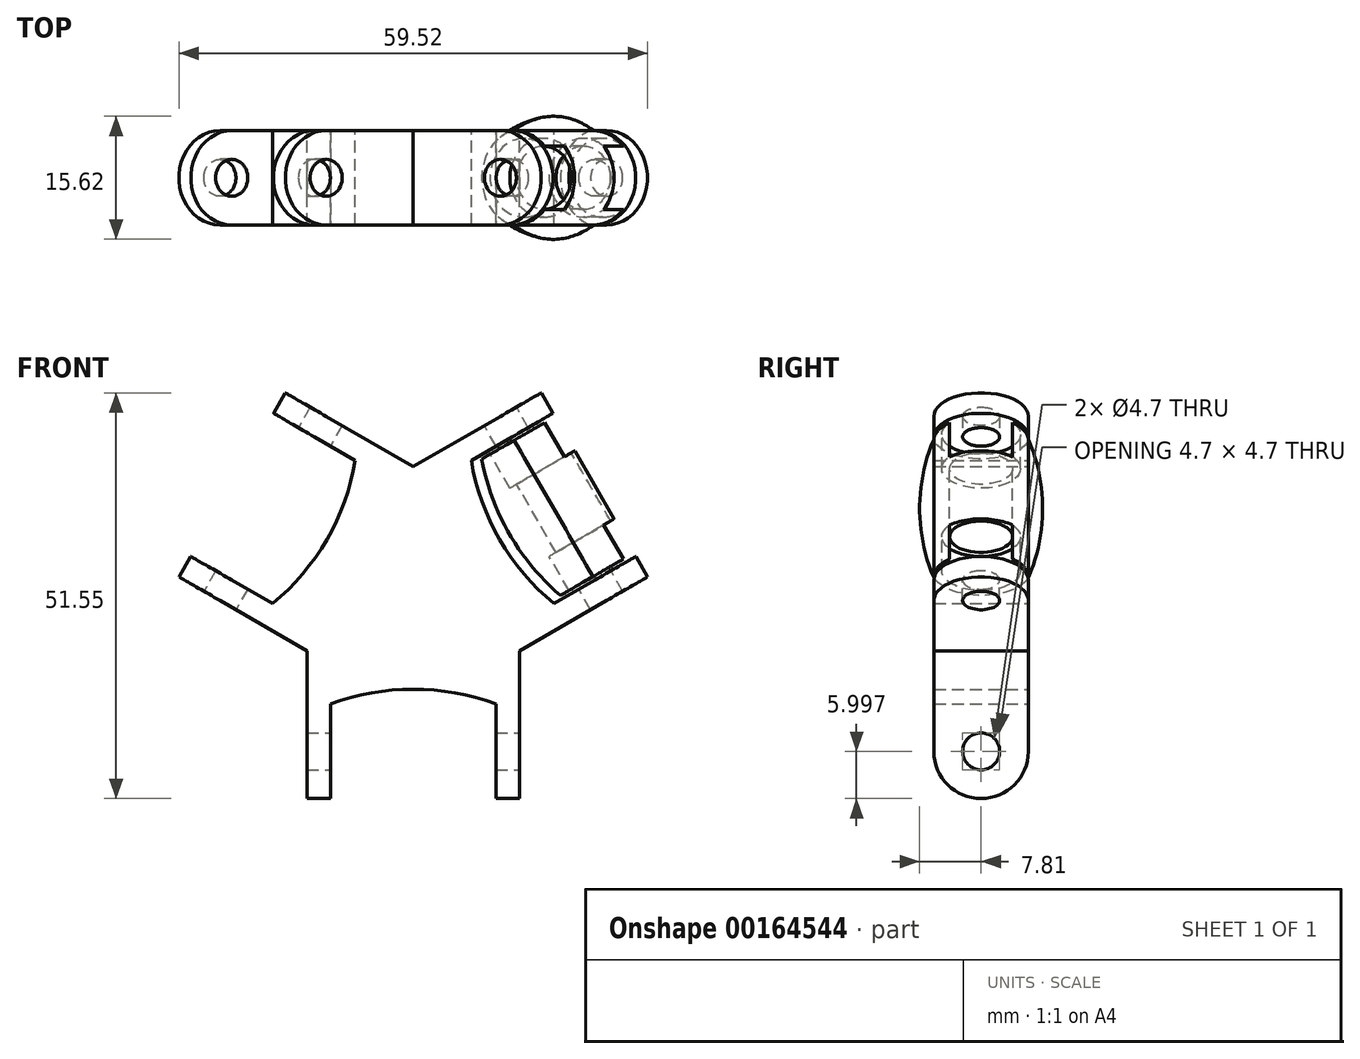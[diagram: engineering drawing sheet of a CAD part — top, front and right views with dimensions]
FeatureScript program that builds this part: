
annotation { "Feature Type Name" : "Feature", "Feature Type Description" : "" }
export const myFeature = defineFeature(function(context is Context, id is Id, definition is map)
    precondition{}
    {
        {
            var Q0;
            Q0=qCreatedBy(makeId("Front.planeOp"),FACE);
            var sketch = newSketch(context, id + "F0", { "sketchPlane" : qUnion([Q0])});
            skCircle(sketch, "E0", {"center": v(0, 0) * mm, "radius": 30 * mm, "construction": true});
            skLineSegment(sketch, "E1", {"start": v(0, 0) * mm, "end": v(0, 27.8) * mm, "construction": true});
            skLineSegment(sketch, "E2", {"start": v(0, 0) * mm, "end": v(24.85, -14.35) * mm, "construction": true});
            skLineSegment(sketch, "E3", {"start": v(38.06, 38.48) * mm, "end": v(52.36, 13.72) * mm, "construction": true});
            skLineSegment(sketch, "E4", {"start": v(0, 0) * mm, "end": v(45.2, 26.1) * mm, "construction": true});
            skLineSegment(sketch, "E5", {"start": v(17.76, 22.38) * mm, "end": v(8.6, 17.09) * mm});
            skLineSegment(sketch, "E6", {"start": v(28.26, 4.2) * mm, "end": v(19.1, -1.1) * mm});
            skArc(sketch, "E7", {"start": v(8.6, 17.09) * mm, "mid": v(12.2, 7.05) * mm, "end": v(19.1, -1.1) * mm, "construction": true});
            skLineSegment(sketch, "E8", {"start": v(19.09, 23.14) * mm, "end": v(24.34, 14.05) * mm, "construction": true});
            skLineSegment(sketch, "E9", {"start": v(24.34, 14.05) * mm, "end": v(29.59, 4.96) * mm, "construction": true});
            skLineSegment(sketch, "E10", {"start": v(13.84, 20.12) * mm, "end": v(24.34, 1.93) * mm, "construction": true});
            skLineSegment(sketch, "E11", {"start": v(13.5, -7.8) * mm, "end": v(21.63, -3.1) * mm, "construction": true});
            skLineSegment(sketch, "E12.MirrorCS", {"start": v(0, 15.59) * mm, "end": v(8.13, 20.28) * mm, "construction": true});
            skPoint(sketch, "E13.center", {"position": v(0.48, 0.8) * mm});
            skLineSegment(sketch, "E13.anchor1", {"start": v(0.48, 0.8) * mm, "end": v(0, 0) * mm, "construction": true});
            skLineSegment(sketch, "E13.anchor2", {"start": v(0.48, 0.8) * mm, "end": v(1.42, 0.8) * mm, "construction": true});
            skLineSegment(sketch, "E14", {"start": v(17.76, 22.38) * mm, "end": v(16.26, 24.98) * mm});
            skLineSegment(sketch, "E15", {"start": v(16.26, 24.98) * mm, "end": v(0, 15.59) * mm});
            skLineSegment(sketch, "E16", {"start": v(8.6, 17.09) * mm, "end": v(7.37, 16.38) * mm});
            skLineSegment(sketch, "E17", {"start": v(19.1, -1.1) * mm, "end": v(17.87, -1.8) * mm});
            skLineSegment(sketch, "E18", {"start": v(28.26, 4.2) * mm, "end": v(29.76, 1.6) * mm});
            skLineSegment(sketch, "E19", {"start": v(29.76, 1.6) * mm, "end": v(13.5, -7.8) * mm});
            skArc(sketch, "E20", {"start": v(7.37, 16.38) * mm, "mid": v(10.98, 6.34) * mm, "end": v(17.87, -1.8) * mm});
            skLineSegment(sketch, "E21.1.0", {"start": v(-29.76, 1.6) * mm, "end": v(-13.5, -7.8) * mm});
            skLineSegment(sketch, "E21.1.1", {"start": v(-28.26, 4.2) * mm, "end": v(-29.76, 1.6) * mm});
            skLineSegment(sketch, "E21.1.2", {"start": v(-28.26, 4.2) * mm, "end": v(-19.1, -1.1) * mm});
            skLineSegment(sketch, "E21.1.3", {"start": v(-19.1, -1.1) * mm, "end": v(-17.87, -1.8) * mm});
            skArc(sketch, "E21.1.4", {"start": v(-17.87, -1.8) * mm, "mid": v(-10.98, 6.34) * mm, "end": v(-7.37, 16.38) * mm});
            skLineSegment(sketch, "E21.1.5", {"start": v(-8.6, 17.09) * mm, "end": v(-7.37, 16.38) * mm});
            skLineSegment(sketch, "E21.1.6", {"start": v(-17.76, 22.38) * mm, "end": v(-8.6, 17.09) * mm});
            skLineSegment(sketch, "E21.1.7", {"start": v(-17.76, 22.38) * mm, "end": v(-16.26, 24.98) * mm});
            skLineSegment(sketch, "E21.1.8", {"start": v(-16.26, 24.98) * mm, "end": v(0, 15.59) * mm});
            skLineSegment(sketch, "E21.2.0", {"start": v(13.5, -26.57) * mm, "end": v(13.5, -7.8) * mm});
            skLineSegment(sketch, "E21.2.1", {"start": v(10.5, -26.57) * mm, "end": v(13.5, -26.57) * mm});
            skLineSegment(sketch, "E21.2.2", {"start": v(10.5, -26.57) * mm, "end": v(10.5, -16) * mm});
            skLineSegment(sketch, "E21.2.3", {"start": v(10.5, -16) * mm, "end": v(10.5, -14.57) * mm});
            skArc(sketch, "E21.2.4", {"start": v(10.5, -14.57) * mm, "mid": v(0, -12.68) * mm, "end": v(-10.5, -14.57) * mm});
            skLineSegment(sketch, "E21.2.5", {"start": v(-10.5, -16) * mm, "end": v(-10.5, -14.57) * mm});
            skLineSegment(sketch, "E21.2.6", {"start": v(-10.5, -26.57) * mm, "end": v(-10.5, -16) * mm});
            skLineSegment(sketch, "E21.2.7", {"start": v(-10.5, -26.57) * mm, "end": v(-13.5, -26.57) * mm});
            skLineSegment(sketch, "E21.2.8", {"start": v(-13.5, -26.57) * mm, "end": v(-13.5, -7.8) * mm});
            skSolve(sketch);
        }
        {
            var Q0;
            Q0=qCreatedBy(makeId("Front.planeOp"),FACE);
            var sketch = newSketch(context, id + "F1", { "sketchPlane" : qUnion([Q0])});
            skLineSegment(sketch, "E22.0", {"start": v(13.84, 20.12) * mm, "end": v(24.34, 1.93) * mm, "construction": true});
            skLineSegment(sketch, "E23.0", {"start": v(19.76, -0.14) * mm, "end": v(17.26, 4.2) * mm});
            skArc(sketch, "E23.1", {"start": v(8.7, 16.57) * mm, "mid": v(12.2, 7.05) * mm, "end": v(18.7, -0.75) * mm});
            skLineSegment(sketch, "E24.trimOffspring", {"start": v(9.76, 17.18) * mm, "end": v(8.7, 16.57) * mm});
            skLineSegment(sketch, "E25.trimOffspring", {"start": v(19.76, -0.14) * mm, "end": v(18.7, -0.75) * mm});
            skLineSegment(sketch, "E26", {"start": v(12.26, 12.85) * mm, "end": v(13.13, 13.35) * mm});
            skLineSegment(sketch, "E27", {"start": v(13.13, 13.35) * mm, "end": v(18.13, 4.7) * mm});
            skLineSegment(sketch, "E28", {"start": v(18.13, 4.7) * mm, "end": v(17.26, 4.2) * mm});
            skLineSegment(sketch, "E29.trimOffspring", {"start": v(12.26, 12.85) * mm, "end": v(9.76, 17.18) * mm});
            skPoint(sketch, "E30.orphan", {"position": v(8.6, 17.09) * mm});
            skSolve(sketch);
        }
        {
            var Q0;
            Q0=qSketchRegion(id+"F1",true);
            var Q1;
            Q1=sQuery(id+"F1.wireOp",EDGE,"E22.0");
            revolve(context, id + "F2", {"entities" : qUnion([Q0]), "axis" : qUnion([Q1]), "revolveType" : RevolveType.FULL});
        }
        {
            var Q0;
            Q0=qSketchRegion(id+"F0",true);
            extrude(context, id + "F3", {"entities" : qUnion([Q0]), "endBound" : BoundingType.SYMMETRIC, "depth" : 12 * mm});
        }
        {
            var Q0;
            Q0=makeQuery(id+"F3.opExtrude","SWEPT_FACE",FACE,{"disambiguationData":[OSD([sQuery(id+"F0.wireOp",EDGE,"E15")])]});
            var sketch = newSketch(context, id + "F4", { "sketchPlane" : qUnion([Q0])});
            skArc(sketch, "E31", {"start": v(20.57, -6) * mm, "mid": v(26.57, 0) * mm, "end": v(20.57, 6) * mm});
            skLineSegment(sketch, "E32", {"start": v(20.57, 6) * mm, "end": v(20.57, 9.05) * mm});
            skLineSegment(sketch, "E33", {"start": v(20.57, 9.05) * mm, "end": v(30.54, 9.05) * mm});
            skLineSegment(sketch, "E34", {"start": v(30.54, 9.05) * mm, "end": v(30.54, -9.05) * mm});
            skLineSegment(sketch, "E35", {"start": v(30.54, -9.05) * mm, "end": v(20.57, -9.05) * mm});
            skLineSegment(sketch, "E36", {"start": v(20.57, -9.05) * mm, "end": v(20.57, -6) * mm});
            skCircle(sketch, "E37", {"center": v(20.57, 0) * mm, "radius": 2.35 * mm});
            skLineSegment(sketch, "E38", {"start": v(0, 19.84) * mm, "end": v(0, -19.76) * mm, "construction": true});
            skSolve(sketch);
        }
        {
            var Q0;
            Q0=qSketchRegion(id+"F4",true);
            extrude(context, id + "F5", {"entities" : qUnion([Q0]), "oppositeDirection" : true, "depth" : 27 * mm});
        }
        {
            var Q0;
            Q0=makeQuery(id+"F5.opExtrude","SWEPT_BODY",BODY,{"disambiguationData":[OSD([sQuery(id+"F4.wireOp",EDGE,"E31"),sQuery(id+"F4.wireOp",EDGE,"E32"),sQuery(id+"F4.wireOp",EDGE,"E33"),sQuery(id+"F4.wireOp",EDGE,"E34"),sQuery(id+"F4.wireOp",EDGE,"E35"),sQuery(id+"F4.wireOp",EDGE,"E36")])]});
            var Q1;
            Q1=makeQuery(id+"F5.opExtrude","SWEPT_BODY",BODY,{"disambiguationData":[OSD([sQuery(id+"F4.wireOp",EDGE,"E37")])]});
            var Q2;
            Q2=sQuery(id+"F0.wireOp",EDGE,"E0");
            circularPattern(context, id + "F6", {"operationType" : NewBodyOperationType.REMOVE, "entities" : qUnion([Q0, Q1]), "axis" : qUnion([Q2]), "angle" : 120 * degree, "instanceCount" : 3});
        }
    });
